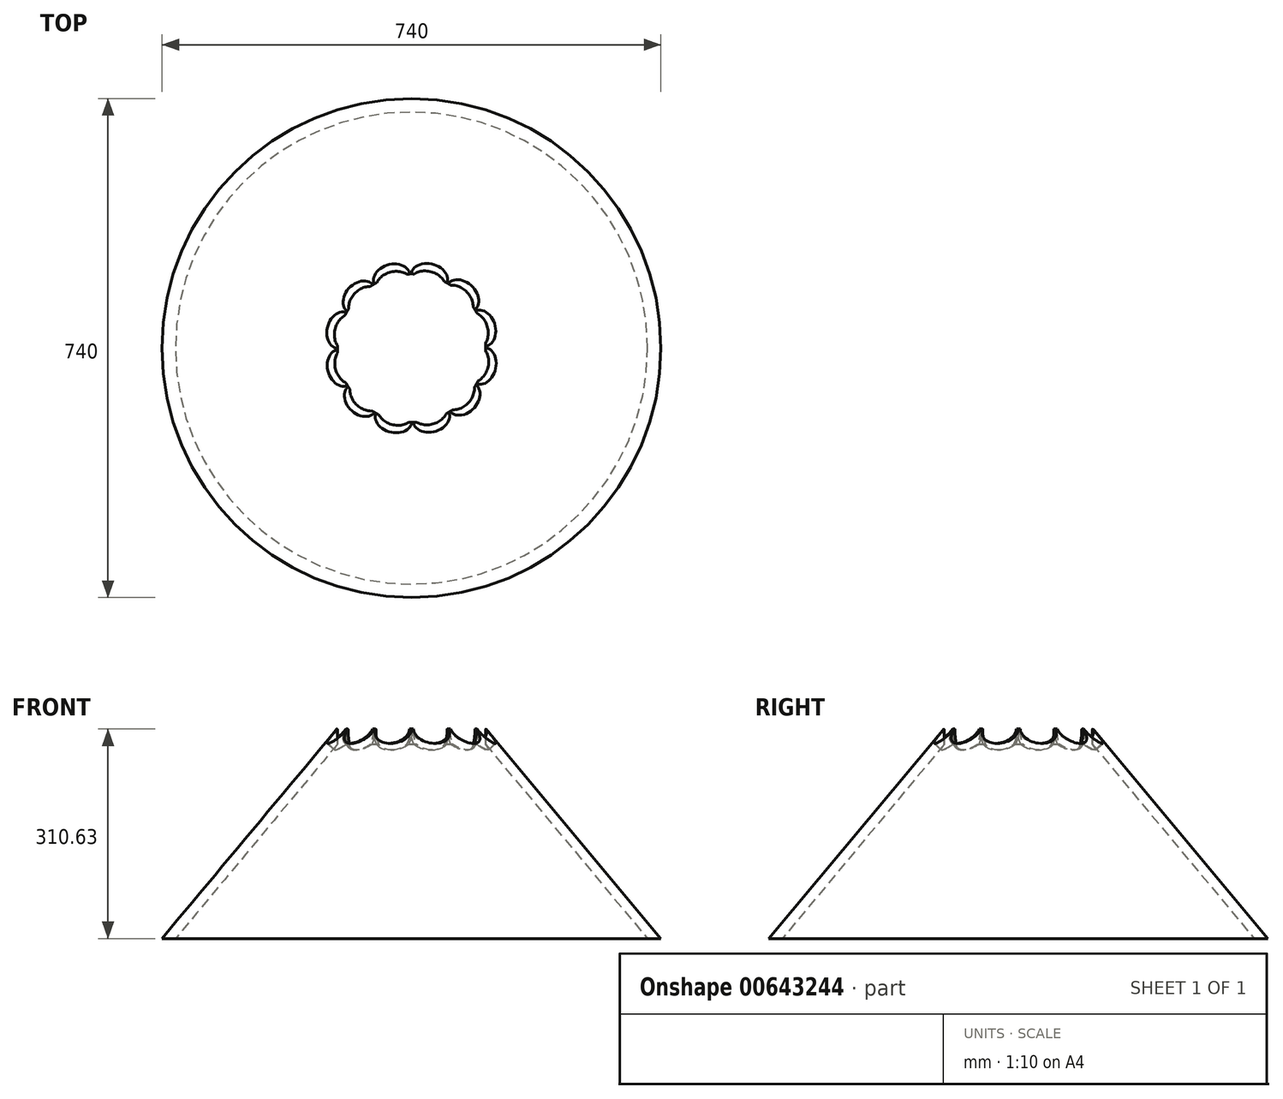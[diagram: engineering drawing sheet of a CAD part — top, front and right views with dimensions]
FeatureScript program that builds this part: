
annotation { "Feature Type Name" : "Feature", "Feature Type Description" : "" }
export const myFeature = defineFeature(function(context is Context, id is Id, definition is map)
    precondition{}
    {
        {
            var Q0;
            Q0=qCreatedBy(makeId("Front.planeOp"),FACE);
            var sketch = newSketch(context, id + "F0", { "sketchPlane" : qUnion([Q0])});
            skLineSegment(sketch, "E0", {"start": v(-100, 300) * mm, "end": v(-350, 0) * mm});
            skLineSegment(sketch, "E1", {"start": v(-350, 0) * mm, "end": v(-370, 0) * mm});
            skLineSegment(sketch, "E2", {"start": v(-370, 0) * mm, "end": v(-110.67, 310.63) * mm});
            skLineSegment(sketch, "E3", {"start": v(-110.67, 310.63) * mm, "end": v(-100, 300) * mm});
            skSolve(sketch);
        }
        {
            var Q0;
            Q0=qCreatedBy(makeId("Front.planeOp"),FACE);
            var sketch = newSketch(context, id + "F1", { "sketchPlane" : qUnion([Q0])});
            skLineSegment(sketch, "E4", {"start": v(0, 0) * mm, "end": v(0, 307.68) * mm});
            skSolve(sketch);
        }
        {
            var Q0;
            Q0=makeQuery(id+"F0.imprint","IMPRINT",FACE,{"disambiguationData":[TD([[makeQuery(id+"F0.imprint","IMPRINT",EDGE,{"derivedFrom":sQuery(id+"F0.wireOp",EDGE,"E0")}),-1.0]])]});
            var Q1;
            Q1=sQuery(id+"F1.wireOp",EDGE,"E4");
            revolve(context, id + "F2", {"entities" : qUnion([Q0]), "axis" : qUnion([Q1]), "revolveType" : RevolveType.ONE_DIRECTION, "angle" : 30 * degree});
        }
        {
            var Q0;
            Q0=qBodyType(qCreatedBy(id+"F1",EDGE),BodyType.WIRE);
            var Q1;
            Q1=qCreatedBy(id+"F4.planeOp",FACE);
            cPlane(context, id + "F3", {"entities" : qUnion([Q0, Q1]), "cplaneType" : CPlaneType.LINE_ANGLE, "offset" : 25 * mm, "angle" : 15 * degree, "width" : 150 * mm, "height" : 150 * mm});
        }
        {
            var Q0;
            Q0=qCreatedBy(id+"F3.planeOp",FACE);
            cPlane(context, id + "F4", {"entities" : qUnion([Q0]), "cplaneType" : CPlaneType.OFFSET, "offset" : 150 * mm, "oppositeDirection" : true, "width" : 150 * mm, "height" : 150 * mm});
        }
        {
            var Q0;
            Q0=qCreatedBy(id+"F4.planeOp",FACE);
            var sketch = newSketch(context, id + "F5", { "sketchPlane" : qUnion([Q0])});
            skLineSegment(sketch, "E5", {"start": v(123.35, 350) * mm, "end": v(-129.89, 350) * mm});
            skSolve(sketch);
        }
        {
            var Q0;
            Q0=qCreatedBy(id+"F4.planeOp",FACE);
            var Q1;
            Q1=qBodyType(qCreatedBy(id+"F5",EDGE),BodyType.WIRE);
            cPlane(context, id + "F6", {"entities" : qUnion([Q0, Q1]), "cplaneType" : CPlaneType.LINE_ANGLE, "offset" : 25 * mm, "angle" : 40 * degree, "oppositeDirection" : true, "width" : 150 * mm, "height" : 150 * mm});
        }
        {
            var Q0;
            Q0=qCreatedBy(id+"F6.planeOp",FACE);
            var sketch = newSketch(context, id + "F7", { "sketchPlane" : qUnion([Q0])});
            skPoint(sketch, "E6", {"position": v(-54.02, 160.46) * mm});
            skPoint(sketch, "E7", {"position": v(0.16, 169.92) * mm});
            skCircle(sketch, "E8", {"center": v(-26.8, 164.42) * mm, "radius": 27.51 * mm});
            skPoint(sketch, "E8.third.point", {"position": v(-23.63, 137.1) * mm});
            skSolve(sketch);
        }
        {
            var Q0;
            Q0=qSketchRegion(id+"F7",true);
            extrude(context, id + "F8", {"entities" : qUnion([Q0]), "operationType" : NewBodyOperationType.REMOVE, "endBound" : BoundingType.SYMMETRIC, "oppositeDirection" : true, "depth" : 300 * mm, "offsetDistance" : 25 * mm});
        }
        {
            var Q0;
            Q0=makeQuery(id+"F2.opRevolve","SWEPT_BODY",BODY,{"disambiguationData":[OSD([sQuery(id+"F0.wireOp",EDGE,"E0"),sQuery(id+"F0.wireOp",EDGE,"E1"),sQuery(id+"F0.wireOp",EDGE,"fKRv1d6K-o61f-OzIg-PQ9P-X68rh1wgNbdu"),sQuery(id+"F0.wireOp",EDGE,"HxRSdhod-90rD-GvnV-GXxi-EBpZglpgOxL8"),sQuery(id+"F0.wireOp",EDGE,"Xlw2WM3j-V6UL-staa-xDYz-mzKcfrXvtrXq")])]});
            var Q1;
            Q1=sQuery(id+"F1.wireOp",EDGE,"E4");
            circularPattern(context, id + "F9", {"operationType" : NewBodyOperationType.ADD, "entities" : qUnion([Q0]), "axis" : qUnion([Q1]), "angle" : 360 * degree, "instanceCount" : 12, "equalSpace" : true});
        }
        {
            var Q0;
            Q0=qCreatedBy(makeId("Front.planeOp"),FACE);
            var sketch = newSketch(context, id + "F10", { "sketchPlane" : qUnion([Q0])});
            skLineSegment(sketch, "E9", {"start": v(-88.86, 366.89) * mm, "end": v(-68.6, 451.64) * mm});
            skLineSegment(sketch, "E10", {"start": v(-68.6, 451.64) * mm, "end": v(-222.9, 443.21) * mm});
            skLineSegment(sketch, "E11", {"start": v(-88.86, 366.89) * mm, "end": v(-155.57, 382.11) * mm});
            skLineSegment(sketch, "E12", {"start": v(-155.57, 382.11) * mm, "end": v(-222.9, 443.21) * mm});
            skSolve(sketch);
        }
        {
            var Q0;
            Q0=makeQuery(id+"F10.imprint","IMPRINT",FACE,{"disambiguationData":[TD([[makeQuery(id+"F10.imprint","IMPRINT",EDGE,{"derivedFrom":sQuery(id+"F10.wireOp",EDGE,"E9")}),1.0]])]});
            var Q1;
            Q1=sQuery(id+"F1.wireOp",EDGE,"E4");
            revolve(context, id + "F11", {"operationType" : NewBodyOperationType.REMOVE, "entities" : qUnion([Q0]), "axis" : qUnion([Q1]), "revolveType" : RevolveType.FULL, "oppositeDirection" : true});
        }
        {
            var Q0;
            Q0=qCreatedBy(makeId("Top.planeOp"),FACE);
            var sketch = newSketch(context, id + "F12", { "sketchPlane" : qUnion([Q0])});
            skCircle(sketch, "E13", {"center": v(0, 0) * mm, "radius": 110 * mm});
            skSolve(sketch);
        }
        {
            var Q0;
            Q0=makeQuery(id+"F12.imprint","IMPRINT",FACE,{"disambiguationData":[TD([[makeQuery(id+"F12.imprint","IMPRINT",EDGE,{"derivedFrom":sQuery(id+"F12.wireOp",EDGE,"E13")}),1.0]])]});
            extrude(context, id + "F13", {"entities" : qUnion([Q0]), "operationType" : NewBodyOperationType.REMOVE, "depth" : 500 * mm, "offsetDistance" : 25 * mm});
        }
    });
